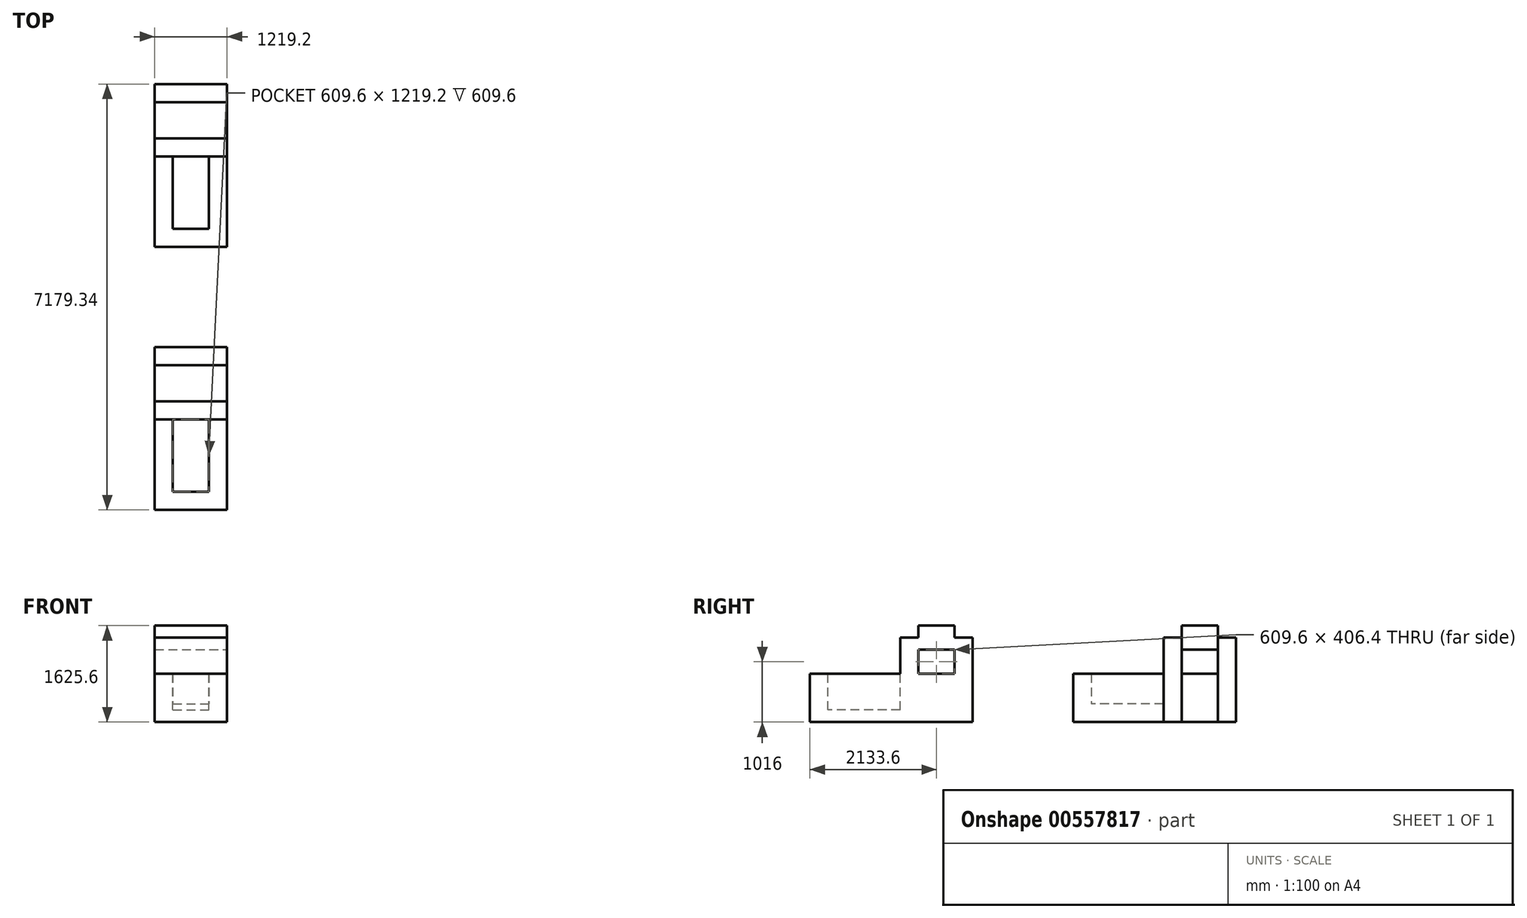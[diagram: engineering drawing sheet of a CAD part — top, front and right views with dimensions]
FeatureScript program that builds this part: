
annotation { "Feature Type Name" : "Feature", "Feature Type Description" : "" }
export const myFeature = defineFeature(function(context is Context, id is Id, definition is map)
    precondition{}
    {
        {
            var Q0;
            Q0=qCreatedBy(makeId("Top.planeOp"),FACE);
            var sketch = newSketch(context, id + "F0", { "sketchPlane" : qUnion([Q0])});
            skLineSegment(sketch, "E0", {"start": v(-96.07, -58.1) * mm, "end": v(1123.13, -58.1) * mm});
            skLineSegment(sketch, "E1", {"start": v(1123.13, -58.1) * mm, "end": v(1123.13, 1465.9) * mm});
            skLineSegment(sketch, "E2", {"start": v(1123.13, 1465.9) * mm, "end": v(818.33, 1465.9) * mm});
            skLineSegment(sketch, "E3", {"start": v(818.33, 1465.9) * mm, "end": v(818.33, 246.7) * mm});
            skLineSegment(sketch, "E4", {"start": v(818.33, 246.7) * mm, "end": v(208.73, 246.7) * mm});
            skLineSegment(sketch, "E5", {"start": v(208.73, 246.7) * mm, "end": v(208.73, 1465.9) * mm});
            skLineSegment(sketch, "E6", {"start": v(208.73, 1465.9) * mm, "end": v(-96.07, 1465.9) * mm});
            skLineSegment(sketch, "E7", {"start": v(-96.07, 1465.9) * mm, "end": v(-96.07, -58.1) * mm});
            skLineSegment(sketch, "E8", {"start": v(-96.07, 1465.9) * mm, "end": v(1123.13, 1465.9) * mm});
            skLineSegment(sketch, "E9", {"start": v(1123.13, 1465.9) * mm, "end": v(1123.13, 2685.1) * mm});
            skLineSegment(sketch, "E10", {"start": v(1123.13, 2685.1) * mm, "end": v(-96.07, 2685.1) * mm});
            skLineSegment(sketch, "E11", {"start": v(-96.07, 2685.1) * mm, "end": v(-96.07, 2380.3) * mm});
            skLineSegment(sketch, "E12", {"start": v(-96.07, 2380.3) * mm, "end": v(1123.13, 2380.3) * mm});
            skLineSegment(sketch, "E13", {"start": v(-96.07, 2380.3) * mm, "end": v(-96.07, 1770.7) * mm});
            skLineSegment(sketch, "E14", {"start": v(-96.07, 1770.7) * mm, "end": v(1123.13, 1770.7) * mm});
            skLineSegment(sketch, "E15", {"start": v(-96.07, 1770.7) * mm, "end": v(-96.07, 1465.9) * mm});
            skSolve(sketch);
        }
        {
            var Q0;
            {var subQ0=sQuery(id+"F0.wireOp",EDGE,"E3");Q0=makeQuery(id+"F0.imprint","IMPRINT",FACE,{"disambiguationData":[TD([[makeQuery(id+"F0.imprint","IMPRINT",EDGE,{"derivedFrom":subQ0}),-1.0]])]});}
            extrude(context, id + "F1", {"entities" : qUnion([Q0]), "depth" : 304.8 * mm, "offsetDistance" : 25.4 * mm});
        }
        {
            var Q0;
            Q0=makeQuery(id+"F0.imprint","IMPRINT",FACE,{"disambiguationData":[TD([[makeQuery(id+"F0.imprint","IMPRINT",EDGE,{"derivedFrom":sQuery(id+"F0.wireOp",EDGE,"E0")}),1.0]])]});
            extrude(context, id + "F2", {"entities" : qUnion([Q0]), "operationType" : NewBodyOperationType.ADD, "depth" : 812.8 * mm, "offsetDistance" : 25.4 * mm});
        }
        {
            var Q0;
            {var subQ3=sQuery(id+"F0.wireOp",EDGE,"E14");Q0=makeQuery(id+"F0.imprint","IMPRINT",FACE,{"disambiguationData":[TD([[makeQuery(id+"F0.imprint","IMPRINT",EDGE,{"derivedFrom":subQ3}),-1.0]])]});}
            var Q1;
            {var subQ0=sQuery(id+"F0.wireOp",EDGE,"E10");Q1=makeQuery(id+"F0.imprint","IMPRINT",FACE,{"disambiguationData":[TD([[makeQuery(id+"F0.imprint","IMPRINT",EDGE,{"derivedFrom":subQ0}),1.0]])]});}
            extrude(context, id + "F3", {"entities" : qUnion([Q0, Q1]), "depth" : 1422.4 * mm, "offsetDistance" : 25.4 * mm});
        }
        {
            var Q0;
            {var subQ0=sQuery(id+"F0.wireOp",EDGE,"E12");Q0=makeQuery(id+"F0.imprint","IMPRINT",FACE,{"disambiguationData":[TD([[makeQuery(id+"F0.imprint","IMPRINT",EDGE,{"derivedFrom":subQ0}),-1.0]])]});}
            extrude(context, id + "F4", {"entities" : qUnion([Q0]), "depth" : 1625.6 * mm, "offsetDistance" : 25.4 * mm});
        }
        {
            var Q0;
            Q0=makeQuery(id+"F4.opExtrude","SWEPT_FACE",FACE,{"disambiguationData":[OSD([sQuery(id+"F0.wireOp",EDGE,"E9")])]});
            var sketch = newSketch(context, id + "F5", { "sketchPlane" : qUnion([Q0])});
            skLineSegment(sketch, "E16", {"start": v(1770.7, 812.8) * mm, "end": v(2380.3, 812.8) * mm});
            skLineSegment(sketch, "E17", {"start": v(2380.3, 812.8) * mm, "end": v(2380.3, 1219.2) * mm});
            skLineSegment(sketch, "E18", {"start": v(2380.3, 1219.2) * mm, "end": v(1770.7, 1219.2) * mm});
            skSolve(sketch);
        }
        {
            var Q0;
            {var subQ0=sQuery(id+"F5.wireOp",EDGE,"E16");Q0=makeQuery(id+"F5.imprint","IMPRINT",FACE,{"disambiguationData":[TD([[makeQuery(id+"F5.imprint","IMPRINT",EDGE,{"derivedFrom":subQ0}),1.0]])]});}
            extrude(context, id + "F6", {"entities" : qUnion([Q0]), "operationType" : NewBodyOperationType.REMOVE, "endBound" : BoundingType.THROUGH_ALL, "oppositeDirection" : true, "depth" : 25.4 * mm, "offsetDistance" : 25.4 * mm});
        }
        {
            var Q0;
            Q0=makeQuery(id+"F2.opExtrude","SWEPT_FACE",FACE,{"disambiguationData":[OSD([sQuery(id+"F0.wireOp",EDGE,"E1")])]});
            var sketch = newSketch(context, id + "F7", { "sketchPlane" : qUnion([Q0])});
            skLineSegment(sketch, "E19", {"start": v(-4494.24, 0) * mm, "end": v(-1751.04, 0) * mm});
            skLineSegment(sketch, "E20", {"start": v(-1751.04, 0) * mm, "end": v(-1751.04, 1422.4) * mm});
            skLineSegment(sketch, "E21", {"start": v(-1751.04, 1422.4) * mm, "end": v(-2055.84, 1422.4) * mm});
            skLineSegment(sketch, "E22", {"start": v(-2055.84, 1422.4) * mm, "end": v(-2055.84, 1625.6) * mm});
            skLineSegment(sketch, "E23", {"start": v(-2055.84, 1625.6) * mm, "end": v(-2665.44, 1625.6) * mm});
            skLineSegment(sketch, "E24", {"start": v(-2665.44, 1625.6) * mm, "end": v(-2665.44, 1422.4) * mm});
            skLineSegment(sketch, "E25", {"start": v(-2665.44, 1422.4) * mm, "end": v(-2970.24, 1422.4) * mm});
            skLineSegment(sketch, "E26", {"start": v(-2970.24, 1422.4) * mm, "end": v(-2970.24, 812.8) * mm});
            skLineSegment(sketch, "E27", {"start": v(-2970.24, 812.8) * mm, "end": v(-4494.24, 812.8) * mm});
            skLineSegment(sketch, "E28", {"start": v(-4494.24, 812.8) * mm, "end": v(-4494.24, 0) * mm});
            skLineSegment(sketch, "E29", {"start": v(-2665.44, 812.8) * mm, "end": v(-2055.84, 812.8) * mm});
            skLineSegment(sketch, "E30", {"start": v(-2055.84, 812.8) * mm, "end": v(-2055.84, 1219.2) * mm});
            skLineSegment(sketch, "E31", {"start": v(-2055.84, 1219.2) * mm, "end": v(-2665.44, 1219.2) * mm});
            skLineSegment(sketch, "E32", {"start": v(-2665.44, 1219.2) * mm, "end": v(-2665.44, 812.8) * mm});
            skSolve(sketch);
        }
        {
            var Q0;
            Q0=makeQuery(id+"F7.imprint","IMPRINT",FACE,{"disambiguationData":[TD([[makeQuery(id+"F7.imprint","IMPRINT",EDGE,{"derivedFrom":sQuery(id+"F7.wireOp",EDGE,"E19")}),1.0]])]});
            extrude(context, id + "F8", {"entities" : qUnion([Q0]), "oppositeDirection" : true, "depth" : 1219.2 * mm, "offsetDistance" : 25.4 * mm});
        }
        {
            var Q0;
            Q0=makeQuery(id+"F8.opExtrude","SWEPT_FACE",FACE,{"disambiguationData":[OSD([sQuery(id+"F7.wireOp",EDGE,"E27")])]});
            var sketch = newSketch(context, id + "F9", { "sketchPlane" : qUnion([Q0])});
            skLineSegment(sketch, "E33", {"start": v(208.73, -2970.24) * mm, "end": v(208.73, -4189.44) * mm});
            skLineSegment(sketch, "E34", {"start": v(208.73, -4189.44) * mm, "end": v(818.33, -4189.44) * mm});
            skLineSegment(sketch, "E35", {"start": v(818.33, -4189.44) * mm, "end": v(818.33, -2970.24) * mm});
            skSolve(sketch);
        }
        {
            var Q0;
            {var subQ0=sQuery(id+"F9.wireOp",EDGE,"E33");Q0=makeQuery(id+"F9.imprint","IMPRINT",FACE,{"disambiguationData":[TD([[makeQuery(id+"F9.imprint","IMPRINT",EDGE,{"derivedFrom":subQ0}),1.0]])]});}
            extrude(context, id + "F10", {"entities" : qUnion([Q0]), "operationType" : NewBodyOperationType.REMOVE, "oppositeDirection" : true, "depth" : 609.6 * mm, "offsetDistance" : 25.4 * mm});
        }
    });
